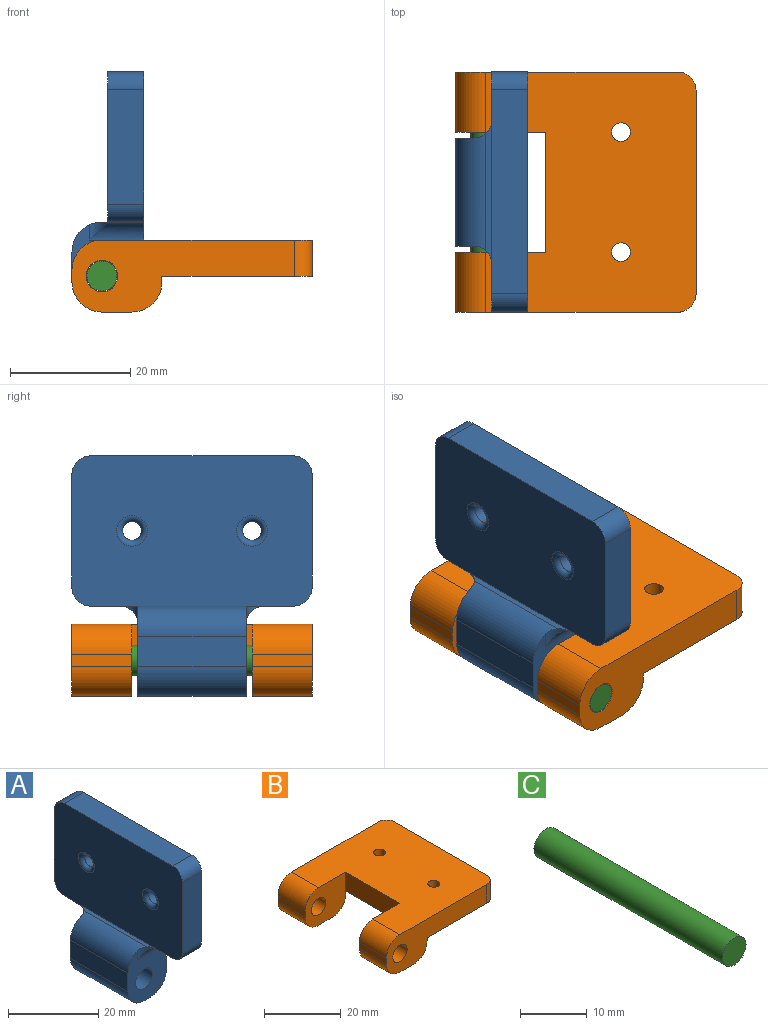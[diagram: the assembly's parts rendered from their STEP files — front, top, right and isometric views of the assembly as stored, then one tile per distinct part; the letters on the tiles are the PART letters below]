
ASSEMBLY  parts=3 mates=2
PART A: 28 faces, bbox 12x40x40 mm
  f0: plane 40x35mm, normal (1,0,0), area 1161mm2, adj f2,f4,f8,f9,f10,f11,f12,f15
  f1: plane 40x25mm, normal (-1,0,0), area 951.4mm2, adj f6,f8,f9,f10,f11,f12,f17,f18
  f2: plane 14.58x12mm, normal (0,-1,0), area 115.1mm2, adj f0,f3,f5,f7,f13,f14,f15,f21
  f3: plane 18x5mm, normal (-1,0,0), area 90mm2, adj f2,f4,f13,f14
  f4: plane 14.58x12mm, normal (0,1,0), area 115.1mm2, adj f0,f3,f5,f7,f13,f14,f15,f16
  f5: plane 18x2mm, normal (0,0,-1), area 36mm2, adj f2,f4,f14,f15
  f6: plane 24x1mm, normal (0,0,1), area 20.9mm2, adj f1,f13,f26,f27
  f7: cylinder r=2.65mm len=18mm, axis (0,1,0), area 299.7mm2, adj f2,f4
  f8: plane 6x5mm, normal (0,0,-1), area 30mm2, adj f0,f1,f20,f21
  f9: plane 6x5mm, normal (0,0,-1), area 30mm2, adj f0,f1,f16,f17
  f10: plane 19x6mm, normal (0,1,0), area 114mm2, adj f0,f1,f17,f18
  f11: plane 34x6mm, normal (0,0,1), area 204mm2, adj f0,f1,f18,f19
  f12: plane 19x6mm, normal (0,-1,0), area 114mm2, adj f0,f1,f19,f20
  f13: cylinder r=5mm len=19.53mm, axis (0,1,0), area 142.3mm2, adj f2,f3,f4,f6,f26,f27
  f14: cylinder r=5mm len=18mm, axis (0,1,0), area 141.4mm2, adj f2,f3,f4,f5
  f15: cylinder r=5mm len=18mm, axis (0,-1,0), area 141.4mm2, adj f0,f2,f4,f5
  f16: cylinder r=3mm len=9mm, axis (-1,0,0), area 33.4mm2, adj f0,f4,f9,f27
  f17: cylinder r=3mm len=6mm, axis (-1,0,0), area 28.3mm2, adj f0,f1,f9,f10
  f18: cylinder r=3mm len=6mm, axis (1,0,0), area 28.3mm2, adj f0,f1,f10,f11
  f19: cylinder r=3mm len=6mm, axis (-1,0,0), area 28.3mm2, adj f0,f1,f11,f12
  f20: cylinder r=3mm len=6mm, axis (1,0,0), area 28.3mm2, adj f0,f1,f8,f12
  f21: cylinder r=3mm len=9mm, axis (1,0,0), area 33.4mm2, adj f0,f2,f8,f26
  f22: cylinder r=1.55mm len=5mm, axis (-1,0,0), area 48.7mm2, adj f0,f24
  f23: cylinder r=1.55mm len=5mm, axis (-1,0,0), area 48.7mm2, adj f0,f25
  f24: torus R=2.55mm, axis (1,0,0), area 18.9mm2, adj f1,f22
  f25: torus R=2.55mm, axis (1,0,0), area 18.9mm2, adj f1,f23
  f26: cylinder r=3mm len=3mm, axis (0,0,-1), area 4.9mm2, adj f2,f6,f13,f21
  f27: cylinder r=3mm len=3mm, axis (0,0,1), area 4.9mm2, adj f4,f6,f13,f16
PART B: 28 faces, bbox 40x40x12 mm
  f0: plane 40x35mm, normal (0,0,1), area 1181mm2, adj f2,f3,f4,f5,f7,f11,f16,f19
  f1: plane 40x25mm, normal (0,0,-1), area 955.3mm2, adj f2,f3,f4,f5,f6,f10,f22,f23
  f2: plane 20x6mm, normal (-1,0,0), area 120mm2, adj f0,f1,f7,f11
  f3: plane 34x6mm, normal (1,0,0), area 204mm2, adj f0,f1,f22,f23
  f4: plane 37x12mm, normal (0,1,0), area 273.8mm2, adj f0,f1,f6,f8,f9,f15,f19,f20
  f5: plane 37x12mm, normal (0,-1,0), area 273.8mm2, adj f0,f1,f10,f12,f13,f14,f16,f17
  f6: plane 10x1mm, normal (1,0,0), area 10mm2, adj f1,f4,f7,f20
  f7: plane 15x12mm, normal (0,-1,0), area 141.8mm2, adj f0,f2,f6,f8,f9,f15,f19,f20
  f8: plane 10x2mm, normal (-1,0,0), area 20mm2, adj f4,f7,f19,f21
  f9: plane 10x5mm, normal (0,0,-1), area 50mm2, adj f4,f7,f20,f21
  f10: plane 10x1mm, normal (1,0,0), area 10mm2, adj f1,f5,f11,f18
  f11: plane 15x12mm, normal (0,1,0), area 141.8mm2, adj f0,f2,f10,f12,f13,f14,f16,f17
  f12: plane 10x2mm, normal (-1,0,0), area 20mm2, adj f5,f11,f16,f17
  f13: plane 10x5mm, normal (0,0,-1), area 50mm2, adj f5,f11,f17,f18
  f14: cylinder r=2.65mm len=10mm, axis (0,-1,0), area 166.5mm2, adj f5,f11
  f15: cylinder r=2.65mm len=10mm, axis (0,-1,0), area 166.5mm2, adj f4,f7
  f16: cylinder r=5mm len=10mm, axis (0,-1,0), area 78.5mm2, adj f0,f5,f11,f12
  f17: cylinder r=5mm len=10mm, axis (0,1,0), area 78.5mm2, adj f5,f11,f12,f13
  f18: cylinder r=5mm len=10mm, axis (0,-1,0), area 78.5mm2, adj f5,f10,f11,f13
  f19: cylinder r=5mm len=10mm, axis (0,-1,0), area 78.5mm2, adj f0,f4,f7,f8
  f20: cylinder r=5mm len=10mm, axis (0,-1,0), area 78.5mm2, adj f4,f6,f7,f9
  f21: cylinder r=5mm len=10mm, axis (0,1,0), area 78.5mm2, adj f4,f7,f8,f9
  f22: cylinder r=3mm len=6mm, axis (0,0,-1), area 28.3mm2, adj f0,f1,f3,f4
  f23: cylinder r=3mm len=6mm, axis (0,0,1), area 28.3mm2, adj f0,f1,f3,f5
  f24: cylinder r=1.55mm len=5mm, axis (0,0,-1), area 48.7mm2, adj f0,f26
  f25: cylinder r=1.55mm len=5mm, axis (0,0,-1), area 48.7mm2, adj f0,f27
  f26: torus R=2.55mm, axis (0,0,1), area 18.9mm2, adj f1,f24
  f27: torus R=2.55mm, axis (0,0,1), area 18.9mm2, adj f1,f25
PART C: 3 faces, bbox 5x40x5 mm
  f0: plane 5x5mm, normal (0,1,0), area 19.6mm2, adj f1
  f1: cylinder r=2.5mm len=40mm, axis (0,-1,0), area 628.3mm2, adj f0,f2
  f2: plane 5x5mm, normal (0,-1,0), area 19.6mm2, adj f1
PLACE A t=(6.03,-18.42,14.47)mm
PLACE B t=(6.03,-18.42,14.47)mm fixed
PLACE C t=(6.03,-18.42,14.47)mm
MATE revolute C.f1 <-> A.f7  axis (0,-1,0) through (-28.97,1.58,14.47)mm
MATE revolute C.f1 <-> B.f14  axis (0,-1,0) through (-28.97,-18.42,14.47)mm
